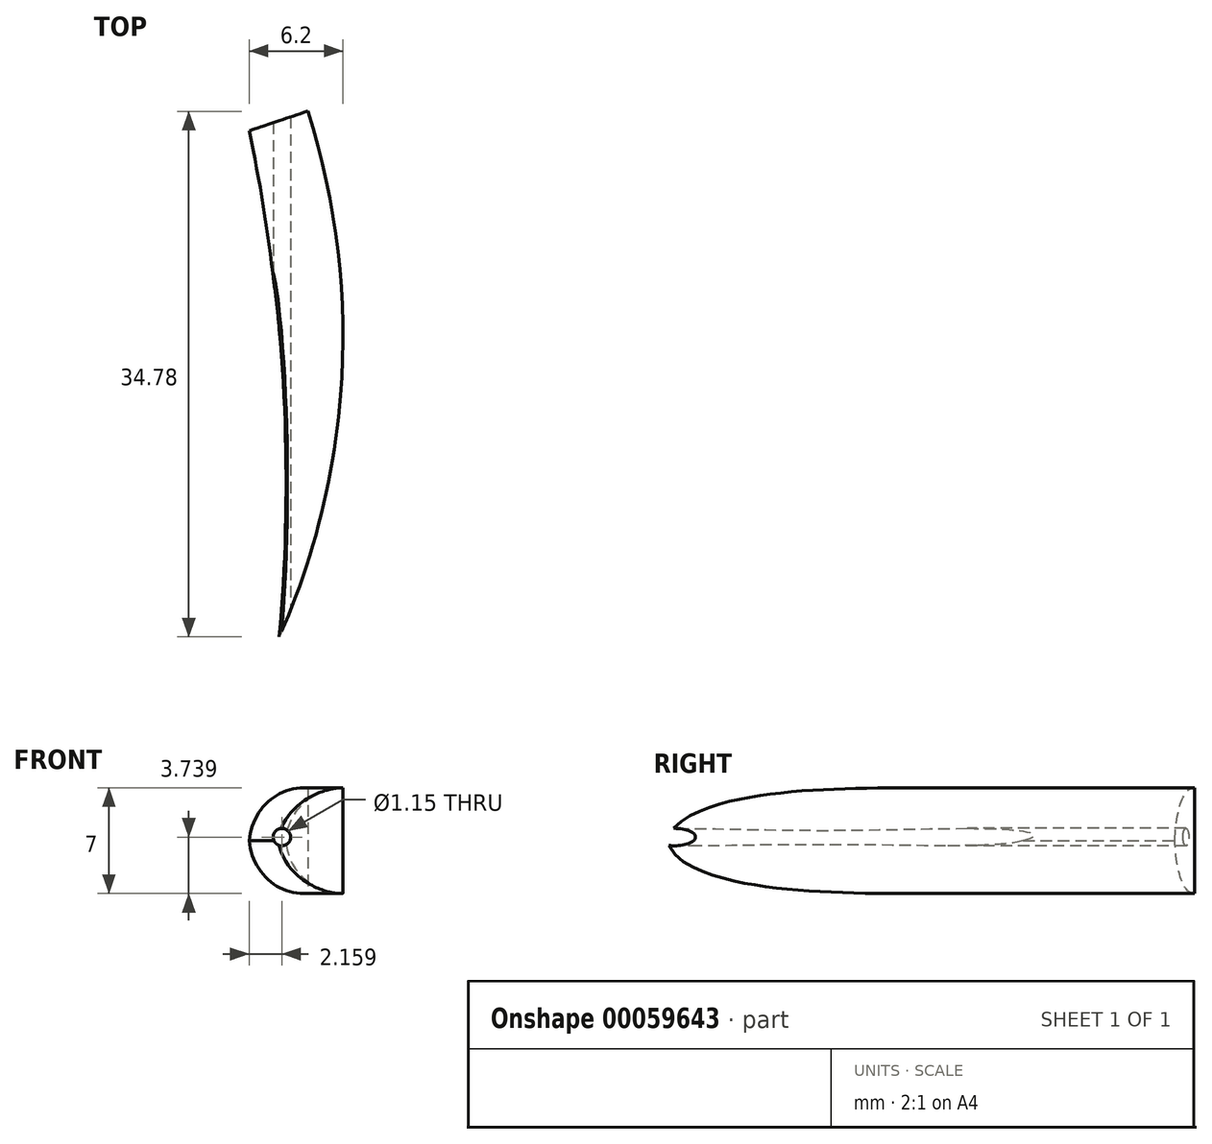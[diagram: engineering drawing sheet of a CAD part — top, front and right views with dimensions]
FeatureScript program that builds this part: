
annotation { "Feature Type Name" : "Feature", "Feature Type Description" : "" }
export const myFeature = defineFeature(function(context is Context, id is Id, definition is map)
    precondition{}
    {
        {
            var Q0;
            Q0=qCreatedBy(makeId("Top.planeOp"),FACE);
            var sketch = newSketch(context, id + "F0", { "sketchPlane" : qUnion([Q0])});
            skLineSegment(sketch, "E0", {"start": v(-59.59, 59.75) * mm, "end": v(-55.71, 61.05) * mm});
            skArc(sketch, "E1", {"start": v(-57.65, 26.13) * mm, "mid": v(-53.46, 43.41) * mm, "end": v(-55.71, 61.05) * mm});
            skPoint(sketch, "E1.startSnap0", {"position": v(-57.65, 60.4) * mm});
            skArc(sketch, "E2", {"start": v(-57.65, 26.13) * mm, "mid": v(-57.37, 43.01) * mm, "end": v(-59.59, 59.75) * mm});
            skSolve(sketch);
        }
        {
            var Q0;
            Q0 = qSketchRegion(id + "F0", true);
            extrude(context, id + "F1", {"entities" : qUnion([Q0]), "depth" : 7 * mm});
        }
        {
            var Q0;
            Q0=makeQuery(id+"F1.opExtrude","CAP_EDGE",EDGE,{"disambiguationData":[OSD([sQuery(id+"F0.wireOp",EDGE,"E2")])],"isStart":false});
            var Q1;
            Q1=makeQuery(id+"F1.opExtrude","CAP_EDGE",EDGE,{"disambiguationData":[OSD([sQuery(id+"F0.wireOp",EDGE,"E2")])],"isStart":true});
            fillet(context, id + "F2", {"entities" : qUnion([Q0, Q1]), "radius" : 3.8 * mm, "tangentPropagation" : true, "allowEdgeOverflow" : false});
        }
        {
            var Q0;
            Q0=qCreatedBy(makeId("Front.planeOp"),FACE);
            var sketch = newSketch(context, id + "F3", { "sketchPlane" : qUnion([Q0])});
            skCircle(sketch, "E3", {"center": v(-57.42, 3.74) * mm, "radius": 0.58 * mm});
            skSolve(sketch);
        }
        {
            var Q0;
            Q0 = qSketchRegion(id + "F3", true);
            extrude(context, id + "F4", {"entities" : qUnion([Q0]), "operationType" : NewBodyOperationType.REMOVE, "oppositeDirection" : true, "depth" : 81.7 * mm});
        }
    });
